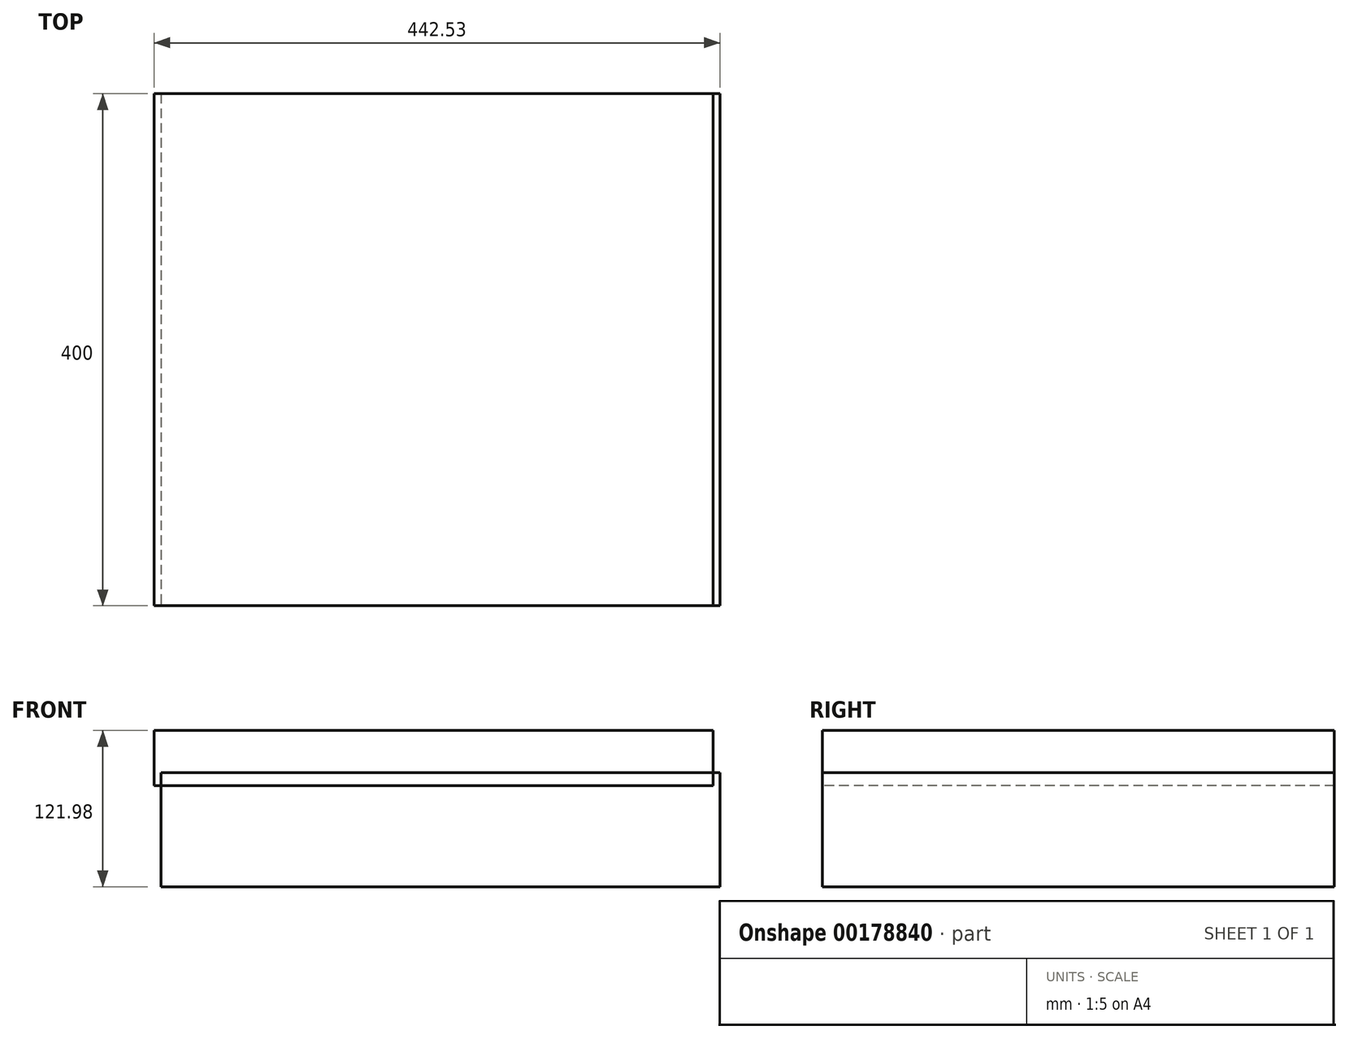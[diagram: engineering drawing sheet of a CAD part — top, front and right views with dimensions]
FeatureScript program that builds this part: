
annotation { "Feature Type Name" : "Feature", "Feature Type Description" : "" }
export const myFeature = defineFeature(function(context is Context, id is Id, definition is map)
    precondition{}
    {
        {
            var Q0;
            Q0=qCreatedBy(makeId("Front.planeOp"),FACE);
            var sketch = newSketch(context, id + "F0", { "sketchPlane" : qUnion([Q0])});
            skLineSegment(sketch, "E0.bottom", {"start": v(-68.93, 62.03) * mm, "end": v(368.07, 62.03) * mm});
            skLineSegment(sketch, "E0.top", {"start": v(-68.93, 19.03) * mm, "end": v(368.07, 19.03) * mm});
            skLineSegment(sketch, "E0.left", {"start": v(-68.93, 62.03) * mm, "end": v(-68.93, 19.03) * mm});
            skLineSegment(sketch, "E0.right", {"start": v(368.07, 62.03) * mm, "end": v(368.07, 19.03) * mm});
            skSolve(sketch);
        }
        {
            var Q0;
            Q0=makeQuery(id+"F0.imprint","IMPRINT",FACE,{"disambiguationData":[TD([[makeQuery(id+"F0.imprint","IMPRINT",EDGE,{"derivedFrom":sQuery(id+"F0.wireOp",EDGE,"E0.bottom")}),-1.0]])]});
            extrude(context, id + "F1", {"entities" : qUnion([Q0]), "oppositeDirection" : true, "offsetDistance" : 25 * mm, "depth" : 400 * mm});
        }
        {
            var Q0;
            Q0=qCreatedBy(makeId("Front.planeOp"),FACE);
            var sketch = newSketch(context, id + "F2", { "sketchPlane" : qUnion([Q0])});
            skLineSegment(sketch, "E1.bottom", {"start": v(-63.4, 29.05) * mm, "end": v(373.6, 29.05) * mm});
            skLineSegment(sketch, "E1.top", {"start": v(-63.4, -59.95) * mm, "end": v(373.6, -59.95) * mm});
            skLineSegment(sketch, "E1.left", {"start": v(-63.4, 29.05) * mm, "end": v(-63.4, -59.95) * mm});
            skLineSegment(sketch, "E1.right", {"start": v(373.6, 29.05) * mm, "end": v(373.6, -59.95) * mm});
            skSolve(sketch);
        }
        {
            var Q0;
            Q0=makeQuery(id+"F2.imprint","IMPRINT",FACE,{"disambiguationData":[TD([[makeQuery(id+"F2.imprint","IMPRINT",EDGE,{"derivedFrom":sQuery(id+"F2.wireOp",EDGE,"E1.bottom")}),-1.0]])]});
            extrude(context, id + "F3", {"entities" : qUnion([Q0]), "oppositeDirection" : true, "depth" : 400 * mm});
        }
    });
